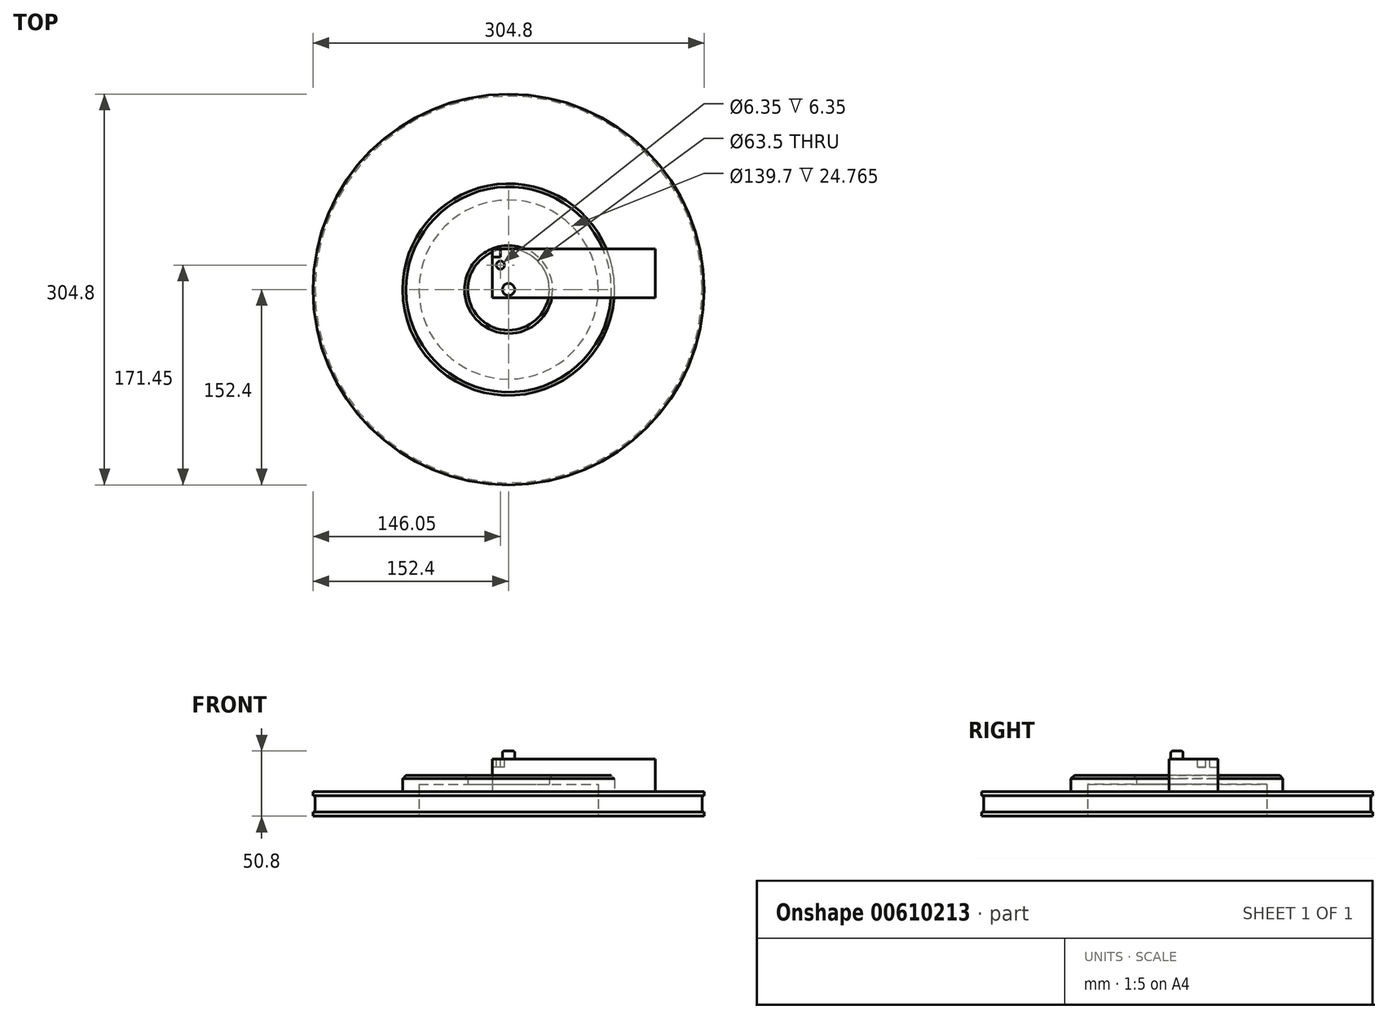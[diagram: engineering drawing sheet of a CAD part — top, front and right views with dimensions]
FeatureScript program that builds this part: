
annotation { "Feature Type Name" : "Feature", "Feature Type Description" : "" }
export const myFeature = defineFeature(function(context is Context, id is Id, definition is map)
    precondition{}
    {
        {
            var Q0;
            Q0=qCreatedBy(makeId("Right.planeOp"),FACE);
            var sketch = newSketch(context, id + "F0", { "sketchPlane" : qUnion([Q0])});
            skLineSegment(sketch, "E0", {"start": v(0, 0) * mm, "end": v(0, 12.7) * mm, "construction": true});
            skLineSegment(sketch, "E1", {"start": v(31.75, 12.7) * mm, "end": v(82.55, 12.7) * mm});
            skLineSegment(sketch, "E2", {"start": v(82.55, 12.7) * mm, "end": v(82.55, 0) * mm});
            skLineSegment(sketch, "E3", {"start": v(82.55, 0) * mm, "end": v(152.4, 0) * mm});
            skLineSegment(sketch, "E4", {"start": v(152.4, 0) * mm, "end": v(152.4, -19.05) * mm});
            skLineSegment(sketch, "E5", {"start": v(152.4, -19.05) * mm, "end": v(69.85, -19.05) * mm});
            skLineSegment(sketch, "E6", {"start": v(69.85, -19.05) * mm, "end": v(69.85, 5.72) * mm});
            skLineSegment(sketch, "E7", {"start": v(69.85, 5.72) * mm, "end": v(31.75, 5.72) * mm});
            skLineSegment(sketch, "E8", {"start": v(31.75, 5.72) * mm, "end": v(31.75, 12.7) * mm});
            skSolve(sketch);
        }
        {
            var Q0;
            Q0=makeQuery(id+"F0.imprint","IMPRINT",FACE,{"disambiguationData":[TD([[makeQuery(id+"F0.imprint","IMPRINT",EDGE,{"derivedFrom":sQuery(id+"F0.wireOp",EDGE,"b49X44rt-f2Xr-CeKm-5HjE-L4sIomjWVCDG")}),1.0]])]});
            var Q1;
            Q1=makeQuery(id+"F0.imprint","IMPRINT",FACE,{"disambiguationData":[TD([[makeQuery(id+"F0.imprint","IMPRINT",EDGE,{"derivedFrom":sQuery(id+"F0.wireOp",EDGE,"E1")}),-1.0]])]});
            var Q2;
            Q2=sQuery(id+"F0.wireOp",EDGE,"E0");
            revolve(context, id + "F1", {"entities" : qUnion([Q0, Q1]), "axis" : qUnion([Q2]), "revolveType" : RevolveType.FULL});
        }
        {
            var Q0;
            Q0=makeQuery(id+"F1.opRevolve","SWEPT_EDGE",EDGE,{"disambiguationData":[OSD([sQuery(id+"F0.wireOp",EDGE,"E1"),sQuery(id+"F0.wireOp",EDGE,"E8")])]});
            var Q1;
            Q1=makeQuery(id+"F1.opRevolve","SWEPT_EDGE",EDGE,{"disambiguationData":[OSD([sQuery(id+"F0.wireOp",EDGE,"E1"),sQuery(id+"F0.wireOp",EDGE,"E2")])]});
            chamfer(context, id + "F2", {"entities" : qUnion([Q0, Q1]), "width" : 2.54 * mm, "tangentPropagation" : true});
        }
        {
            var Q0;
            Q0=qCreatedBy(makeId("Top.planeOp"),FACE);
            var sketch = newSketch(context, id + "F3", { "sketchPlane" : qUnion([Q0])});
            skLineSegment(sketch, "E9.bottom", {"start": v(114.3, -6.35) * mm, "end": v(-12.7, -6.35) * mm});
            skLineSegment(sketch, "E9.top", {"start": v(114.3, 31.75) * mm, "end": v(-12.7, 31.75) * mm});
            skLineSegment(sketch, "E9.left", {"start": v(114.3, -6.35) * mm, "end": v(114.3, 31.75) * mm});
            skLineSegment(sketch, "E9.right", {"start": v(-12.7, -6.35) * mm, "end": v(-12.7, 31.75) * mm});
            skPoint(sketch, "E9.middle", {"position": v(50.8, 12.7) * mm});
            skSolve(sketch);
        }
        {
            var Q0;
            Q0=makeQuery(id+"F3.imprint","IMPRINT",FACE,{"disambiguationData":[TD([[makeQuery(id+"F3.imprint","IMPRINT",EDGE,{"derivedFrom":sQuery(id+"F3.wireOp",EDGE,"E9.bottom")}),-1.0]])]});
            extrude(context, id + "F4", {"entities" : qUnion([Q0]), "depth" : 25.4 * mm, "offsetDistance" : 25.4 * mm});
        }
        {
            var Q0;
            Q0=makeQuery(id+"F4.opExtrude","CAP_FACE",FACE,{"disambiguationData":[OSD([sQuery(id+"F3.wireOp",EDGE,"E9.bottom"),sQuery(id+"F3.wireOp",EDGE,"E9.top"),sQuery(id+"F3.wireOp",EDGE,"E9.left"),sQuery(id+"F3.wireOp",EDGE,"E9.right")])],"isStart":false});
            var sketch = newSketch(context, id + "F5", { "sketchPlane" : qUnion([Q0])});
            skCircle(sketch, "E10", {"center": v(0, 0) * mm, "radius": 4.76 * mm});
            skSolve(sketch);
        }
        {
            var Q0;
            Q0=makeQuery(id+"F5.imprint","IMPRINT",FACE,{"disambiguationData":[TD([[makeQuery(id+"F5.imprint","IMPRINT",EDGE,{"derivedFrom":sQuery(id+"F5.wireOp",EDGE,"E10")}),1.0]])]});
            extrude(context, id + "F6", {"entities" : qUnion([Q0]), "operationType" : NewBodyOperationType.ADD, "depth" : 6.35 * mm, "offsetDistance" : 25.4 * mm});
        }
        {
            var Q0;
            Q0=makeQuery(id+"F4.opExtrude","CAP_FACE",FACE,{"disambiguationData":[OSD([sQuery(id+"F3.wireOp",EDGE,"E9.bottom"),sQuery(id+"F3.wireOp",EDGE,"E9.top"),sQuery(id+"F3.wireOp",EDGE,"E9.left"),sQuery(id+"F3.wireOp",EDGE,"E9.right")])],"isStart":false});
            var sketch = newSketch(context, id + "F7", { "sketchPlane" : qUnion([Q0])});
            skLineSegment(sketch, "E11.bottom", {"start": v(-12.7, 31.75) * mm, "end": v(-6.35, 31.75) * mm});
            skLineSegment(sketch, "E11.top", {"start": v(-12.7, 25.4) * mm, "end": v(-6.35, 25.4) * mm});
            skLineSegment(sketch, "E11.left", {"start": v(-12.7, 31.75) * mm, "end": v(-12.7, 25.4) * mm});
            skLineSegment(sketch, "E11.right", {"start": v(-6.35, 31.75) * mm, "end": v(-6.35, 25.4) * mm});
            skSolve(sketch);
        }
        {
            var Q0;
            Q0=makeQuery(id+"F7.imprint","IMPRINT",FACE,{"disambiguationData":[TD([[makeQuery(id+"F7.imprint","IMPRINT",EDGE,{"derivedFrom":sQuery(id+"F7.wireOp",EDGE,"E11.bottom")}),1.0]])]});
            extrude(context, id + "F8", {"entities" : qUnion([Q0]), "operationType" : NewBodyOperationType.REMOVE, "oppositeDirection" : true, "depth" : 6.35 * mm, "offsetDistance" : 25.4 * mm});
        }
        {
            var Q0;
            Q0=makeQuery(id+"F4.opExtrude","CAP_FACE",FACE,{"disambiguationData":[OSD([sQuery(id+"F3.wireOp",EDGE,"E9.bottom"),sQuery(id+"F3.wireOp",EDGE,"E9.top"),sQuery(id+"F3.wireOp",EDGE,"E9.left"),sQuery(id+"F3.wireOp",EDGE,"E9.right")])],"isStart":false});
            var sketch = newSketch(context, id + "F9", { "sketchPlane" : qUnion([Q0])});
            skCircle(sketch, "E12", {"center": v(-6.35, 19.05) * mm, "radius": 3.18 * mm});
            skSolve(sketch);
        }
        {
            var Q0;
            Q0=makeQuery(id+"F9.imprint","IMPRINT",FACE,{"disambiguationData":[TD([[makeQuery(id+"F9.imprint","IMPRINT",EDGE,{"derivedFrom":sQuery(id+"F9.wireOp",EDGE,"E12")}),1.0]])]});
            extrude(context, id + "F10", {"entities" : qUnion([Q0]), "operationType" : NewBodyOperationType.REMOVE, "oppositeDirection" : true, "depth" : 6.35 * mm, "offsetDistance" : 25.4 * mm});
        }
        {
            var Q0;
            Q0=makeQuery(id+"F6.opExtrude","CAP_EDGE",EDGE,{"disambiguationData":[OSD([sQuery(id+"F5.wireOp",EDGE,"E10")])],"isStart":false});
            fillet(context, id + "F11", {"entities" : qUnion([Q0]), "radius" : 1.27 * mm, "tangentPropagation" : true, "allowEdgeOverflow" : false});
        }
        {
            var Q0;
            Q0=qCreatedBy(makeId("Front.planeOp"),FACE);
            var sketch = newSketch(context, id + "F12", { "sketchPlane" : qUnion([Q0])});
            skLineSegment(sketch, "E13.bottom", {"start": v(6.35, -3.18) * mm, "end": v(-6.35, -3.18) * mm});
            skLineSegment(sketch, "E13.top", {"start": v(6.35, -15.88) * mm, "end": v(-6.35, -15.88) * mm});
            skLineSegment(sketch, "E13.left", {"start": v(6.35, -3.18) * mm, "end": v(6.35, -15.88) * mm});
            skLineSegment(sketch, "E13.right", {"start": v(-6.35, -3.18) * mm, "end": v(-6.35, -15.88) * mm});
            skPoint(sketch, "E13.middle", {"position": v(0, -9.53) * mm});
            skSolve(sketch);
        }
        {
            var Q0;
            Q0=qCreatedBy(makeId("Right.planeOp"),FACE);
            var sketch = newSketch(context, id + "F13", { "sketchPlane" : qUnion([Q0])});
            skLineSegment(sketch, "E14.0", {"start": v(0, -3.18) * mm, "end": v(0, -15.88) * mm});
            skLineSegment(sketch, "E15", {"start": v(-152.4, -19.05) * mm, "end": v(-152.4, 0) * mm, "construction": true});
            skLineSegment(sketch, "E16.bottom", {"start": v(-150.81, -3.18) * mm, "end": v(-153.99, -3.18) * mm});
            skLineSegment(sketch, "E16.top", {"start": v(-150.81, -15.88) * mm, "end": v(-153.99, -15.88) * mm});
            skLineSegment(sketch, "E16.left", {"start": v(-150.81, -3.18) * mm, "end": v(-150.81, -15.88) * mm});
            skLineSegment(sketch, "E16.right", {"start": v(-153.99, -3.18) * mm, "end": v(-153.99, -15.88) * mm});
            skPoint(sketch, "E16.middle", {"position": v(-152.4, -9.53) * mm});
            skSolve(sketch);
        }
        {
            var Q0;
            Q0=makeQuery(id+"F13.imprint","IMPRINT",FACE,{"disambiguationData":[TD([[makeQuery(id+"F13.imprint","IMPRINT",EDGE,{"derivedFrom":sQuery(id+"F13.wireOp",EDGE,"E16.bottom")}),1.0]])]});
            var Q1;
            Q1=sQuery(id+"F13.wireOp",EDGE,"E14.0");
            revolve(context, id + "F14", {"operationType" : NewBodyOperationType.REMOVE, "entities" : qUnion([Q0]), "axis" : qUnion([Q1]), "revolveType" : RevolveType.FULL, "oppositeDirection" : true});
        }
    });
